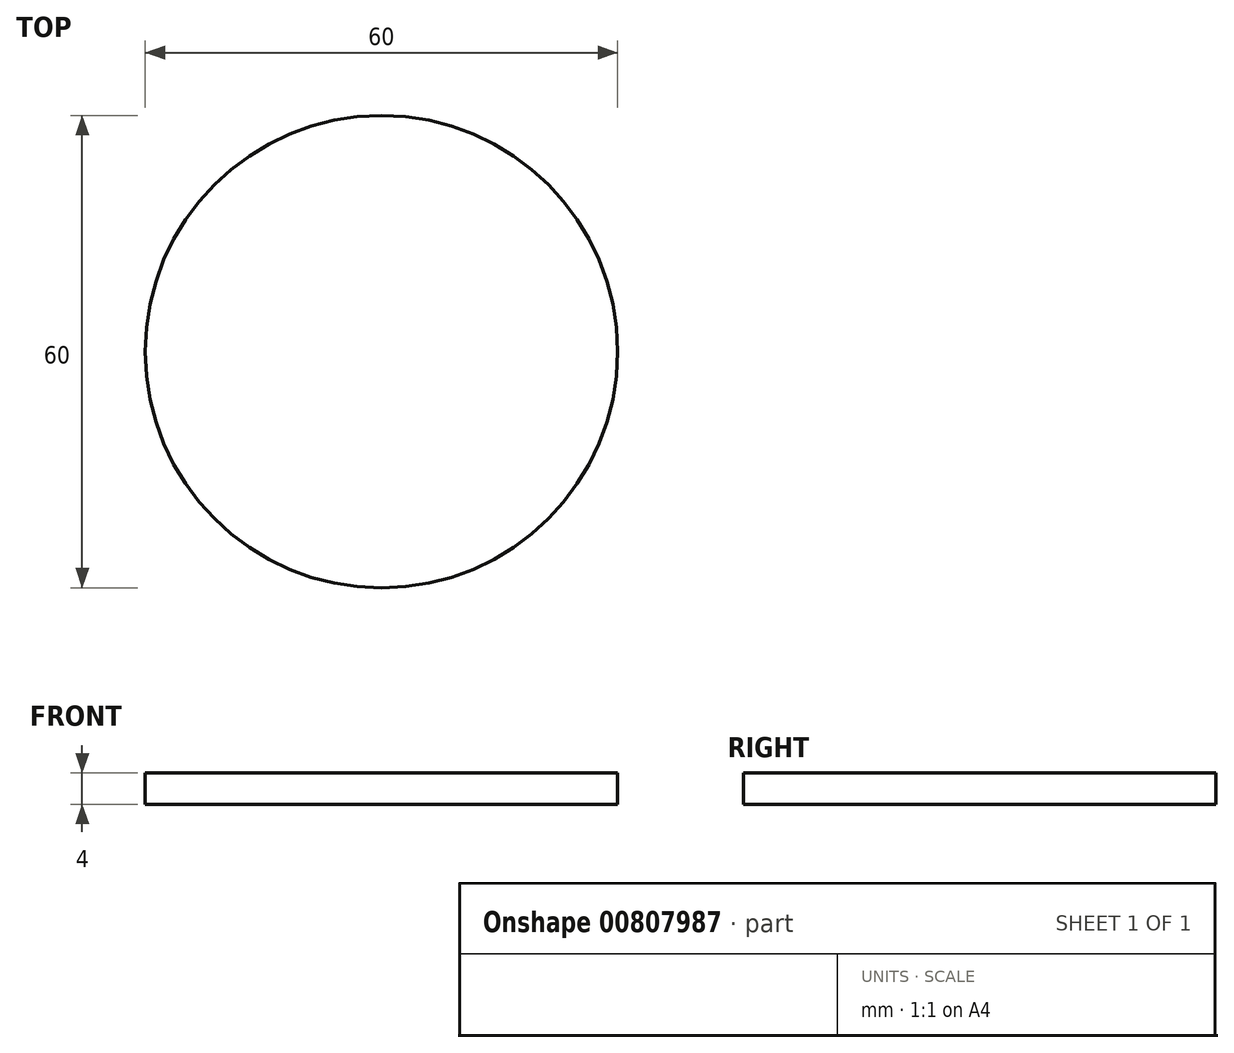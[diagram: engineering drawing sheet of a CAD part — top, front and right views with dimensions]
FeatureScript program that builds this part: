
annotation { "Feature Type Name" : "Feature", "Feature Type Description" : "" }
export const myFeature = defineFeature(function(context is Context, id is Id, definition is map)
    precondition{}
    {
        {
            var Q0;
            Q0=qCreatedBy(makeId("Top.planeOp"),FACE);
            var sketch = newSketch(context, id + "F0", { "sketchPlane" : qUnion([Q0])});
            skCircle(sketch, "E0", {"center": v(0, 0) * mm, "radius": 30 * mm});
            skCircle(sketch, "E1", {"center": v(0, 0) * mm, "radius": 6 * mm});
            skSolve(sketch);
        }
        {
            var Q0;
            Q0=makeQuery(id+"F0.imprint","IMPRINT",FACE,{"disambiguationData":[TD([[makeQuery(id+"F0.imprint","IMPRINT",EDGE,{"derivedFrom":sQuery(id+"F0.wireOp",EDGE,"E0")}),1.0]])]});
            var Q1;
            Q1=makeQuery(id+"F0.imprint","IMPRINT",FACE,{"disambiguationData":[TD([[makeQuery(id+"F0.imprint","IMPRINT",EDGE,{"derivedFrom":sQuery(id+"F0.wireOp",EDGE,"E1")}),1.0]])]});
            extrude(context, id + "F1", {"entities" : qUnion([Q0, Q1]), "oppositeDirection" : true, "depth" : 4 * mm, "offsetDistance" : 25 * mm});
        }
    });
